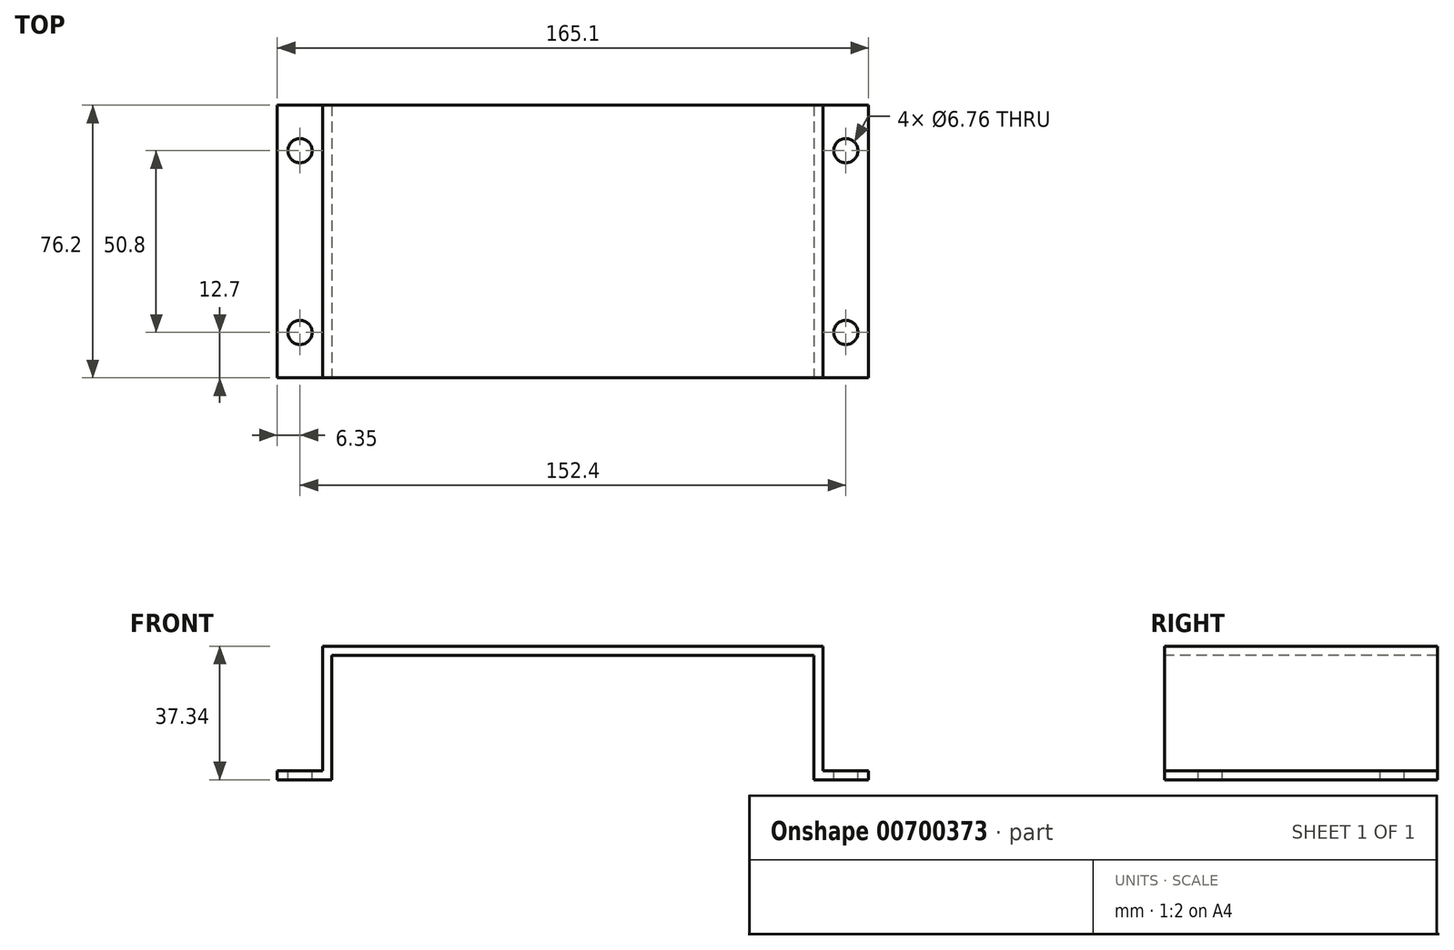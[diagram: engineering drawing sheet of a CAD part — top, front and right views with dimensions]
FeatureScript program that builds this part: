
annotation { "Feature Type Name" : "Feature", "Feature Type Description" : "" }
export const myFeature = defineFeature(function(context is Context, id is Id, definition is map)
    precondition{}
    {
        {
            var Q0;
            Q0=qCreatedBy(makeId("Front.planeOp"),FACE);
            var sketch = newSketch(context, id + "F0", { "sketchPlane" : qUnion([Q0])});
            skLineSegment(sketch, "E0.bottom", {"start": v(0, 0) * mm, "end": v(15.24, 0) * mm});
            skLineSegment(sketch, "E0.top", {"start": v(0, 2.54) * mm, "end": v(12.7, 2.54) * mm});
            skLineSegment(sketch, "E0.left", {"start": v(0, 0) * mm, "end": v(0, 2.54) * mm});
            skLineSegment(sketch, "E0.right", {"start": v(165.1, 0) * mm, "end": v(165.1, 2.54) * mm});
            skLineSegment(sketch, "E1.top", {"start": v(12.7, 37.34) * mm, "end": v(152.4, 37.34) * mm});
            skLineSegment(sketch, "E1.left", {"start": v(12.7, 2.54) * mm, "end": v(12.7, 37.34) * mm});
            skLineSegment(sketch, "E1.right", {"start": v(152.4, 2.54) * mm, "end": v(152.4, 37.34) * mm});
            skLineSegment(sketch, "E2.trimOffspring", {"start": v(152.4, 2.54) * mm, "end": v(165.1, 2.54) * mm});
            skLineSegment(sketch, "E3.0", {"start": v(149.86, 0) * mm, "end": v(149.86, 34.8) * mm});
            skLineSegment(sketch, "E3.1", {"start": v(15.24, 34.8) * mm, "end": v(149.86, 34.8) * mm});
            skLineSegment(sketch, "E3.2", {"start": v(15.24, 0) * mm, "end": v(15.24, 34.8) * mm});
            skLineSegment(sketch, "E4.trimOffspring", {"start": v(149.86, 0) * mm, "end": v(165.1, 0) * mm});
            skSolve(sketch);
        }
        {
            var Q0;
            Q0 = qSketchRegion(id + "F0", true);
            extrude(context, id + "F1", {"entities" : qUnion([Q0]), "oppositeDirection" : true, "depth" : 76.2 * mm, "offsetDistance" : 25.4 * mm});
        }
        {
            var Q0;
            Q0=makeQuery(id+"F1.opExtrude","SWEPT_FACE",FACE,{"disambiguationData":[OSD([sQuery(id+"F0.wireOp",EDGE,"E0.top")])]});
            var sketch = newSketch(context, id + "F2", { "sketchPlane" : qUnion([Q0])});
            skPoint(sketch, "E5", {"position": v(6.35, 63.5) * mm});
            skPoint(sketch, "E6", {"position": v(6.35, 12.7) * mm});
            skPoint(sketch, "E7", {"position": v(158.75, 63.5) * mm});
            skPoint(sketch, "E8", {"position": v(158.75, 12.7) * mm});
            skLineSegment(sketch, "E9", {"start": v(6.35, 76.2) * mm, "end": v(6.35, 0) * mm, "construction": true});
            skLineSegment(sketch, "E10", {"start": v(158.75, 76.2) * mm, "end": v(158.75, 0) * mm, "construction": true});
            skSolve(sketch);
        }
        {
            var Q0;
            Q0=sQuery(id+"F2.wireOp",VERTEX,"E7");
            var Q1;
            Q1=sQuery(id+"F2.wireOp",VERTEX,"E8");
            var Q2;
            Q2=sQuery(id+"F2.wireOp",VERTEX,"E6");
            var Q3;
            Q3=sQuery(id+"F2.wireOp",VERTEX,"E5");
            var Q4;
            Q4=makeQuery(id+"F1.opExtrude","SWEPT_BODY",BODY,{"disambiguationData":[OSD([sQuery(id+"F0.wireOp",EDGE,"E0.bottom"),sQuery(id+"F0.wireOp",EDGE,"E0.top"),sQuery(id+"F0.wireOp",EDGE,"E0.left"),sQuery(id+"F0.wireOp",EDGE,"E0.right"),sQuery(id+"F0.wireOp",EDGE,"E1.top"),sQuery(id+"F0.wireOp",EDGE,"E1.left"),sQuery(id+"F0.wireOp",EDGE,"E1.right"),sQuery(id+"F0.wireOp",EDGE,"E2.trimOffspring"),sQuery(id+"F0.wireOp",EDGE,"E3.0"),sQuery(id+"F0.wireOp",EDGE,"E3.1"),sQuery(id+"F0.wireOp",EDGE,"E3.2"),sQuery(id+"F0.wireOp",EDGE,"E4.trimOffspring")])]});
            hole(context, id + "F3", {"style" : HoleStyle.SIMPLE, "endStyle" : HoleEndStyle.THROUGH, "standardTappedOrClearance" : lookupTablePath({ "standard" : "ANSI", "fit" : "Normal (ASME)", "size" : "1/4", "type" : "Clearance" }), "standardBlindInLast" : lookupTablePath({ "fit" : "Free", "standard" : "ANSI", "size" : "1/4", "type" : "Clearance" }), "holeDiameter" : 6.76 * mm, "majorDiameter" : 6.35 * mm, "isTappedThrough" : true, "tappedDepth" : 10.32 * mm, "tapClearance" : 3, "startFromSketch" : true, "locations" : qUnion([Q0, Q1, Q2, Q3]), "scope" : qUnion([Q4])});
        }
    });
